# Revit family: NX-EOF-MC-01
name_source: partatom
category: Communication Devices
units: mm (PartAtom-declared; Revit-internal decimal feet)

## family parameters
Cut with Voids When Loaded = No
Host = Face
Maintain Annotation Orientation = No
OmniClass Number = 23.85.80.11.27
OmniClass Title = Lighting Controls
Part Type = Normal
Room Calculation Point = No
Round Connector Dimension = Use Diameter
Shared = Yes

## types (1)
- NX-EOF-MC-01
    Assembly Code = D5090
    Black = Paint -  Carbon Black
    Certifications = Conforms with UL, CE, FCC Class A
    Default Elevation = 48 "
    Description = The NX Media Converter allows a transition from copper based ethernet to fiber. When laying ethernet cables outside of a building, it is necessary to use fiber for a safe and reliable operation of a networked system. The NX Media Converter allows contractors to connect to NX based lighting control networks across multiple buildings with complete confidence.
    Features = • Supports 10BASE-T, 100BASE-TX, 100BASE-FX and IEEE 802.3 specification
• Multimode converter, supports up to 5km distance
• Cost-effective, small and lightweight
• RJ45 port supports Full/Half-Duplex auto-negotiation and MDI/MDIX
auto-crossover
• 120V AC Power Supply
• LED indicators for RJ45 and fiber port status
• 0º to 40ºC Operating Temperature
• Wall mounting kit included
    Height = 3.77 "
    Manufacturer = NX Lighting Controls
    Model = NX–EOF–MC–01
    Type Comments = NX Media Converter
    URL = https://www.currentlighting.com
    Warranty = 5-Years Warranty
    White = Paint -  Machined Aluminum
    Width = 1.71 "

## geometry (parser evidence)
native form markers: Sweep x1
no freeform markers — native parametric forms only
